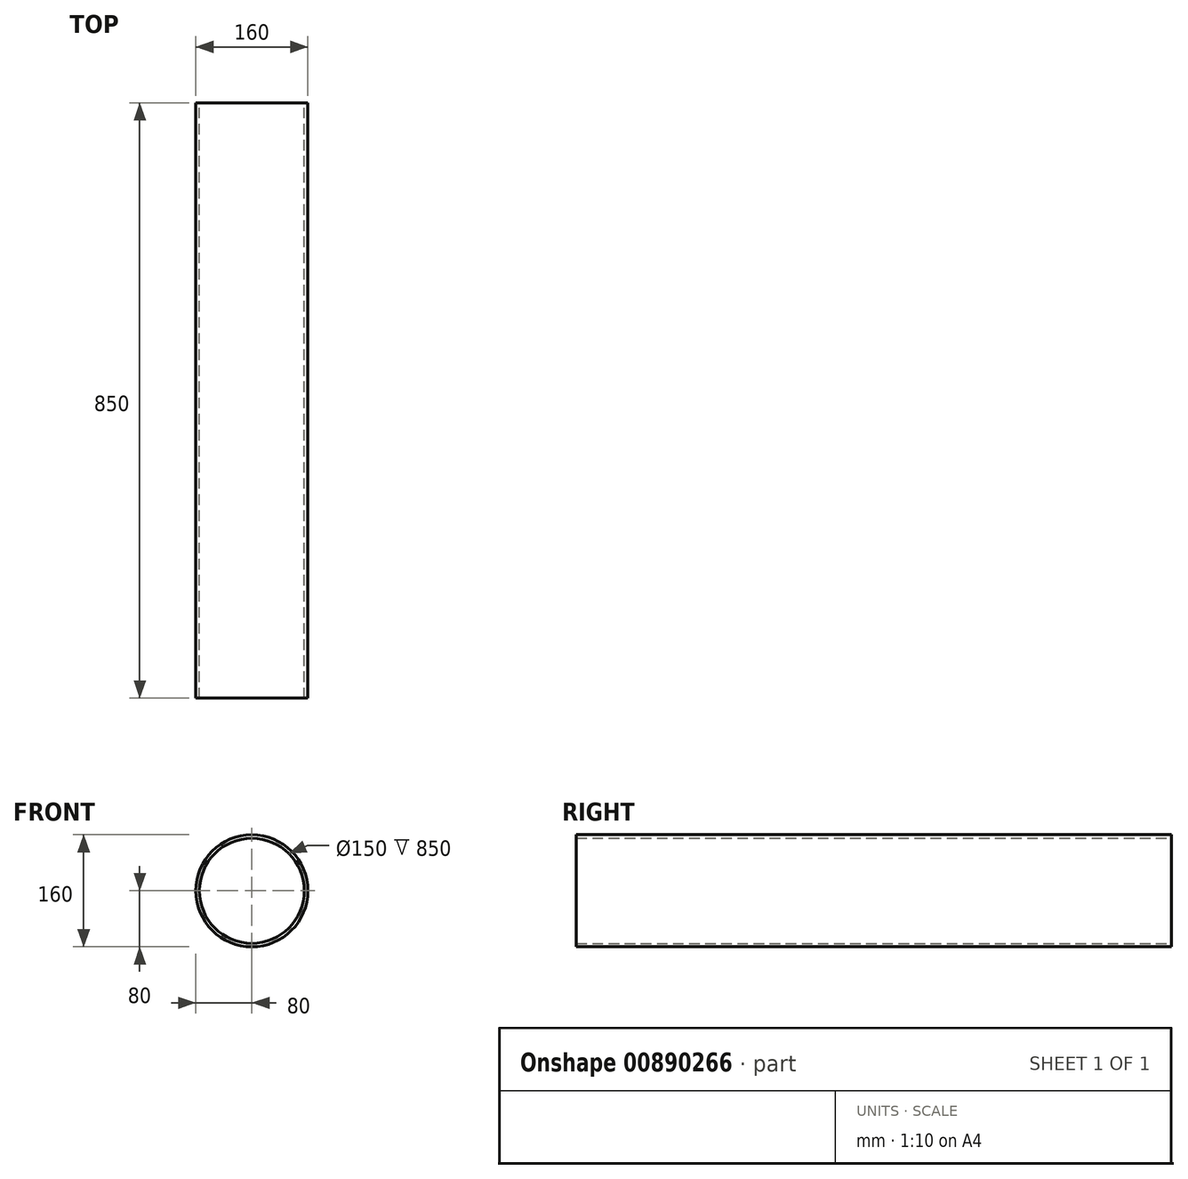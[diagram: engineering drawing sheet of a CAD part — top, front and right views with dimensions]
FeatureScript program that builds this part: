
annotation { "Feature Type Name" : "Feature", "Feature Type Description" : "" }
export const myFeature = defineFeature(function(context is Context, id is Id, definition is map)
    precondition{}
    {
        {
            var Q0;
            Q0=qCreatedBy(makeId("Front.planeOp"),FACE);
            var sketch = newSketch(context, id + "F0", { "sketchPlane" : qUnion([Q0])});
            skCircle(sketch, "E0", {"center": v(0, 0) * mm, "radius": 80 * mm});
            skCircle(sketch, "E1", {"center": v(0, 0) * mm, "radius": 75 * mm});
            skSolve(sketch);
        }
        {
            var Q0;
            Q0=makeQuery(id+"F0.imprint","IMPRINT",FACE,{"disambiguationData":[TD([[makeQuery(id+"F0.imprint","IMPRINT",EDGE,{"derivedFrom":sQuery(id+"F0.wireOp",EDGE,"E0")}),1.0]])]});
            extrude(context, id + "F1", {"entities" : qUnion([Q0]), "depth" : 850 * mm, "offsetDistance" : 25 * mm});
        }
    });
